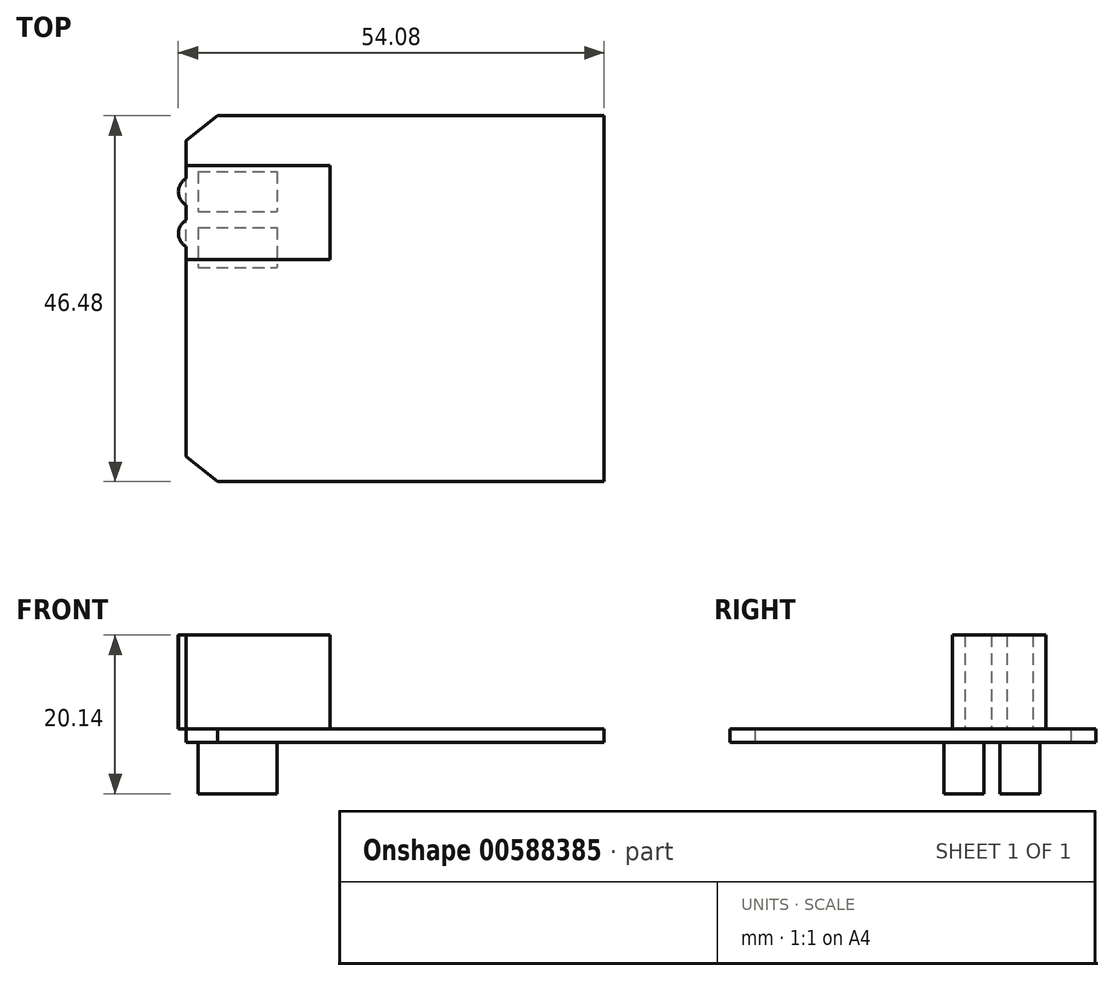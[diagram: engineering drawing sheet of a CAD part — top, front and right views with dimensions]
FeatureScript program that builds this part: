
annotation { "Feature Type Name" : "Feature", "Feature Type Description" : "" }
export const myFeature = defineFeature(function(context is Context, id is Id, definition is map)
    precondition{}
    {
        {
            var Q0;
            Q0=qCreatedBy(makeId("Top.planeOp"),FACE);
            var sketch = newSketch(context, id + "F0", { "sketchPlane" : qUnion([Q0])});
            skLineSegment(sketch, "E0.bottom", {"start": v(26.54, -23.24) * mm, "end": v(-22.58, -23.24) * mm});
            skLineSegment(sketch, "E0.top", {"start": v(26.54, 23.24) * mm, "end": v(-22.58, 23.24) * mm});
            skLineSegment(sketch, "E0.left", {"start": v(26.54, -23.24) * mm, "end": v(26.54, 23.24) * mm});
            skLineSegment(sketch, "E0.right", {"start": v(-26.54, -20.06) * mm, "end": v(-26.54, 20.06) * mm});
            skPoint(sketch, "E0.middle", {"position": v(0, 0) * mm});
            skLineSegment(sketch, "E1", {"start": v(-26.54, 20.06) * mm, "end": v(-22.58, 23.24) * mm});
            skLineSegment(sketch, "E2", {"start": v(-22.58, -23.24) * mm, "end": v(-26.54, -20.06) * mm});
            skSolve(sketch);
        }
        {
            var Q0;
            Q0 = qSketchRegion(id + "F0", true);
            extrude(context, id + "F1", {"entities" : qUnion([Q0]), "depth" : 1.68 * mm, "offsetDistance" : 25.4 * mm});
        }
        {
            var Q0;
            Q0=makeQuery(id+"F1.opExtrude","CAP_FACE",FACE,{"disambiguationData":[OSD([sQuery(id+"F0.wireOp",EDGE,"E0.bottom"),sQuery(id+"F0.wireOp",EDGE,"E0.top"),sQuery(id+"F0.wireOp",EDGE,"E0.left"),sQuery(id+"F0.wireOp",EDGE,"E0.right"),sQuery(id+"F0.wireOp",EDGE,"E1"),sQuery(id+"F0.wireOp",EDGE,"E2")])],"isStart":false});
            var sketch = newSketch(context, id + "F2", { "sketchPlane" : qUnion([Q0])});
            skLineSegment(sketch, "E3", {"start": v(-26.54, 5) * mm, "end": v(-8.25, 5) * mm});
            skLineSegment(sketch, "E4", {"start": v(-8.25, 5) * mm, "end": v(-8.25, 16.9) * mm});
            skLineSegment(sketch, "E5", {"start": v(-8.26, 16.9) * mm, "end": v(-26.54, 16.9) * mm});
            skLineSegment(sketch, "E6", {"start": v(-26.54, 16.9) * mm, "end": v(-26.54, 15.27) * mm});
            skArc(sketch, "E7", {"start": v(-26.54, 9.97) * mm, "mid": v(-27.53, 8.3) * mm, "end": v(-26.54, 6.63) * mm});
            skArc(sketch, "E8.MirrorCS", {"start": v(-26.54, 11.92) * mm, "mid": v(-27.53, 13.59) * mm, "end": v(-26.54, 15.26) * mm});
            skArc(sketch, "E9.MirrorCS", {"start": v(-26.54, 11.92) * mm, "mid": v(-27.54, 13.6) * mm, "end": v(-26.54, 15.27) * mm});
            skLineSegment(sketch, "E10.trimOffspring", {"start": v(-26.54, 11.92) * mm, "end": v(-26.54, 9.97) * mm});
            skLineSegment(sketch, "E11.trimOffspring", {"start": v(-26.54, 6.63) * mm, "end": v(-26.54, 5) * mm});
            skSolve(sketch);
        }
        {
            var Q0;
            Q0 = qSketchRegion(id + "F2", true);
            extrude(context, id + "F3", {"entities" : qUnion([Q0]), "depth" : 11.94 * mm, "offsetDistance" : 25.4 * mm});
        }
        {
            var Q0;
            Q0=makeQuery(id+"F1.opExtrude","CAP_FACE",FACE,{"disambiguationData":[OSD([sQuery(id+"F0.wireOp",EDGE,"E0.bottom"),sQuery(id+"F0.wireOp",EDGE,"E0.top"),sQuery(id+"F0.wireOp",EDGE,"E0.left"),sQuery(id+"F0.wireOp",EDGE,"E0.right"),sQuery(id+"F0.wireOp",EDGE,"E1"),sQuery(id+"F0.wireOp",EDGE,"E2")])],"isStart":true});
            var sketch = newSketch(context, id + "F4", { "sketchPlane" : qUnion([Q0])});
            skLineSegment(sketch, "E12.bottom", {"start": v(-25, -16.14) * mm, "end": v(-14.98, -16.14) * mm});
            skLineSegment(sketch, "E12.top", {"start": v(-25, -11.06) * mm, "end": v(-14.98, -11.06) * mm});
            skLineSegment(sketch, "E12.left", {"start": v(-25, -16.14) * mm, "end": v(-25, -11.06) * mm});
            skLineSegment(sketch, "E12.right", {"start": v(-14.98, -16.14) * mm, "end": v(-14.98, -11.06) * mm});
            skLineSegment(sketch, "E13", {"start": v(-25, -11.06) * mm, "end": v(-25, -9.02) * mm});
            skLineSegment(sketch, "E14.bottom", {"start": v(-25, -9.02) * mm, "end": v(-14.98, -9.02) * mm});
            skLineSegment(sketch, "E14.top", {"start": v(-25, -3.94) * mm, "end": v(-14.98, -3.94) * mm});
            skLineSegment(sketch, "E14.left", {"start": v(-25, -9.02) * mm, "end": v(-25, -3.94) * mm});
            skLineSegment(sketch, "E14.right", {"start": v(-14.98, -9.02) * mm, "end": v(-14.98, -3.94) * mm});
            skSolve(sketch);
        }
        {
            var Q0;
            Q0 = qSketchRegion(id + "F4", true);
            extrude(context, id + "F5", {"entities" : qUnion([Q0]), "depth" : 6.53 * mm, "offsetDistance" : 25.4 * mm});
        }
    });
